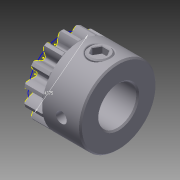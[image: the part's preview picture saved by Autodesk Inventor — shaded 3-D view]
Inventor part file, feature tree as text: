
AUTODESK INVENTOR PART (.ipt)
format: ipt  version: 2012 (Build 160160000, 160)  size: 579,584 bytes
history: native  units: in
note: dims shown in document units (in); Inventor stores cm internally (conversion verified against a paired STEP export)
features: imported_body x2, sketch x1
ambient origin geometry x8: Origin, YZ Plane, XZ Plane, XY Plane, X Axis, Y Axis, Z Axis, Center Point
feature tree (3):
  sketch  "Sketch1"  dims[d0=0.4375in]
  imported_body  "Base1"
  imported_body  "Base2"
